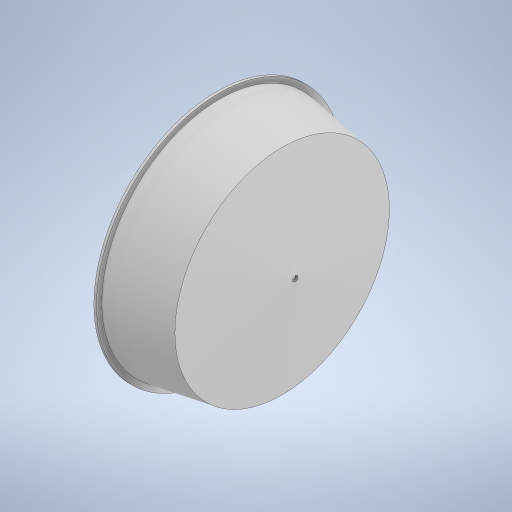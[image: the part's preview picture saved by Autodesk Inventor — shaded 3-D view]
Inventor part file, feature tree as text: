
AUTODESK INVENTOR PART (.ipt)
format: ipt  version: 2023.2 (Build 272271000, 271)  size: 261,120 bytes
history: native  units: mm
features: revolve x1, sketch x1
ambient origin geometry x8: Origin, YZ Plane, XZ Plane, XY Plane, X Axis, Y Axis, Z Axis, Center Point
bodies: Solid1 (feature_tree)
feature tree (2):
  revolve  "Revolution1"  [1 undecoded]
  sketch  "Sketch1"  dims[d5=360.0deg d7=15.0mm d11=2.0mm d12=0.5mm d13=1.0mm d17=20.0mm d19=12.0mm d20=0.5mm d21=0.5mm]
note: 1 required parameter value undecoded (feature->parameter linkage not recoverable at this tier; creation-order binding heuristic only, values carry confidence <= 0.55)
